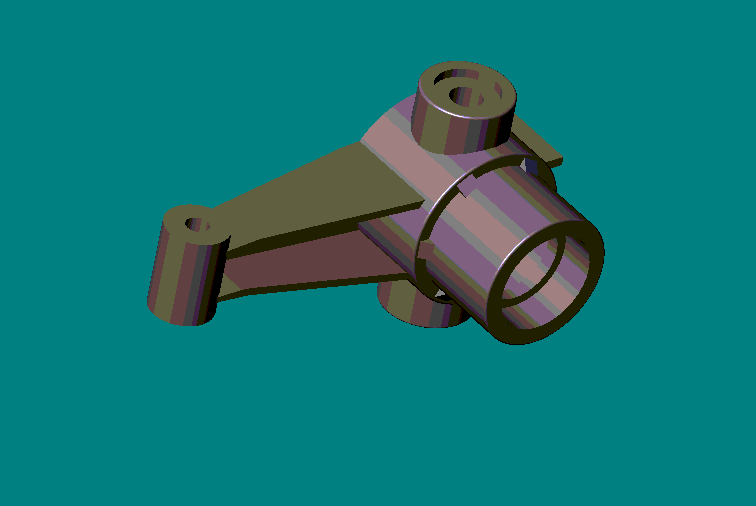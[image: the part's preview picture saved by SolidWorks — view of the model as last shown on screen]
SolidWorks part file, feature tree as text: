
SOLIDWORKS PART (.sldprt)
format: sldprt  version: not decoded by parser v0  size: 336,896 bytes
history: native  units: mm
features: sketch x16, cut_extrude x10, extrude x6, plane x4, material x1, pattern_circular x1, fillet x1, mirror x1 (+8 scaffold rows collapsed)
feature tree (48):
  scaffold x8  (default folders/planes/origin — collapsed)
  material  "Matériau <non spécifié>"
  plane  "Plane1"
  plane  "Plane2"
  plane  "Plane3"
  sketch  "Esquisse1"  dims[D1=20.0mm D2=18.0mm D3=42.0mm D4=18.0mm D5=3.0mm D6=6.0mm D7=11.0mm]
  extrude  "Base-Extrusion"  Depth=10mm
  sketch  "Esquisse2"  dims[D1=8.0mm D2=4.0mm]
  cut_extrude  "Enlèv. mat.-Extru.1"  [1 undecoded]
  sketch  "Esquisse3"  dims[c1.D2=18.0mm c1.D3=18.0mm c1.D1=32.0mm c2.D3=9.5mm c2.D2=32.0mm]
  extrude  "Boss.-Extru.1"  Depth=12.5mm
  sketch  "Esquisse4"  dims[D1=15.0mm]
  extrude  "Boss.-Extru.2"  Depth=10mm
  sketch  "Esquisse5"  dims[D1=7.0mm]
  extrude  "Boss.-Extru.3"  Depth=10mm
  sketch  "Esquisse6"  dims[D1=13.0mm]
  sketch  "Esquisse9"  dims[D2=10.0mm D1=6.0mm]
  extrude  "Boss.-Extru.4"  Depth=26mm
  cut_extrude  "Enlèv. mat.-Extru.3"  Depth=13mm
  sketch  "Esquisse10"  dims[D1=11.0mm]
  cut_extrude  "Enlèv. mat.-Extru.4"  Depth=4mm
  sketch  "Esquisse11"  dims[D1=11.0mm]
  cut_extrude  "Enlèv. mat.-Extru.5"  Depth=4mm
  sketch  "Esquisse12"  dims[D1=9.0mm]
  cut_extrude  "Enlèv. mat.-Extru.6"  [1 undecoded]
  sketch  "Esquisse15"  dims[D1=7.0mm D2=1.5mm D3=1.5mm]
  extrude  "Boss.-Extru.5"  Depth=2mm
  pattern_circular  "Répétition circulaire1"  Count=6 Angle=60deg
  fillet  "Congé3"  Radius=0.25mm
  sketch  "Esquisse16"  dims[D1=7.0mm]
  cut_extrude  "Enlèv. mat.-Extru.7"  Depth=1mm
  sketch  "Esquisse17"  dims[D1=3.5mm]
  cut_extrude  "Enlèv. mat.-Extru.8"  Depth=5mm
  mirror  "Symétrie1"
  sketch  "Esquisse18"  dims[D1=2.5mm]
  cut_extrude  "Enlèv. mat.-Extru.9"  [1 undecoded]
  plane  "Plan1"  Offset=15mm
  sketch  "Esquisse19"
  cut_extrude  "Enlèv. mat.-Extru.11"  Depth=12mm
  sketch  "Esquisse21"
  cut_extrude  "Enlèv. mat.-Extru.13"  Depth=5mm
decode coverage: 29 of 35 modeling features carry decoded parameters
note: 3 parameter values undecoded
summary: no parameter record found for 3 features
note: suppression state not decoded; provenance and decode notes live in map.json
